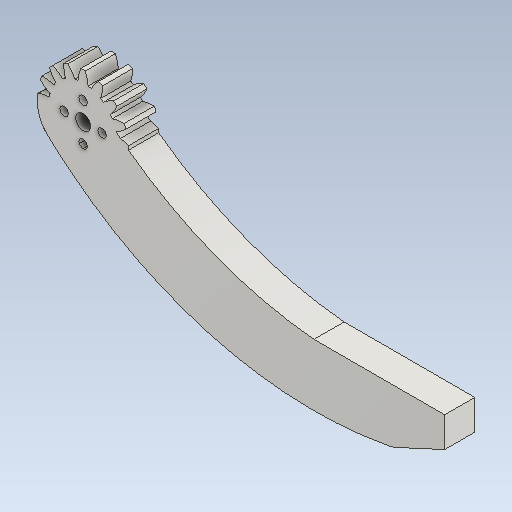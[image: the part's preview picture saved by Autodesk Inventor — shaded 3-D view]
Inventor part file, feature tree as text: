
AUTODESK INVENTOR PART (.ipt)
format: ipt  version: 2020 (Build 240168000, 168)  size: 228,352 bytes
history: native  units: in
note: dims shown in document units (in); Inventor stores cm internally (conversion verified against a paired STEP export)
features: sketch x13, other x12, plane x3
ambient origin geometry x8: Origin, YZ Plane, XZ Plane, XY Plane, X Axis, Y Axis, Z Axis, Center Point
bodies: Solid1 (feature_tree)
feature tree (28):
  other  "Spur Gear1"
  other  "Solid1::Spur Gear1"
  other  "TaggingFeature1"
  sketch  "Sketch1"  dims[d0=0.3937in]
  sketch  "Sketch2"  dims[d9=0.0in d14=0.0in d15=1.3416in d16=0.0in d17=0.0in d18=0.0in d19=1.3416in]
  sketch  "Sketch3"
  sketch  "Sketch4"
  sketch  "Sketch6"
  sketch  "Sketch7"
  sketch  "Sketch8"
  sketch  "Sketch9"
  sketch  "Sketch11"
  sketch  "Sketch12"
  sketch  "Sketch13"
  sketch  "Sketch15"
  sketch  "Sketch17"
  plane  "XZ Plane_1"
  plane  "Work Plane2"
  plane  "Work Plane3"
  other  "Srf1"
  other  "Srf1::Derived"
  other  "Start plane iMate"
  other  "Distance iMate"
  other  "Position iMate"
  other  "Mesh iMate"
  other  "Axis iMate"
  other  "Mesh iMate2"
  other  "Align iMate"
